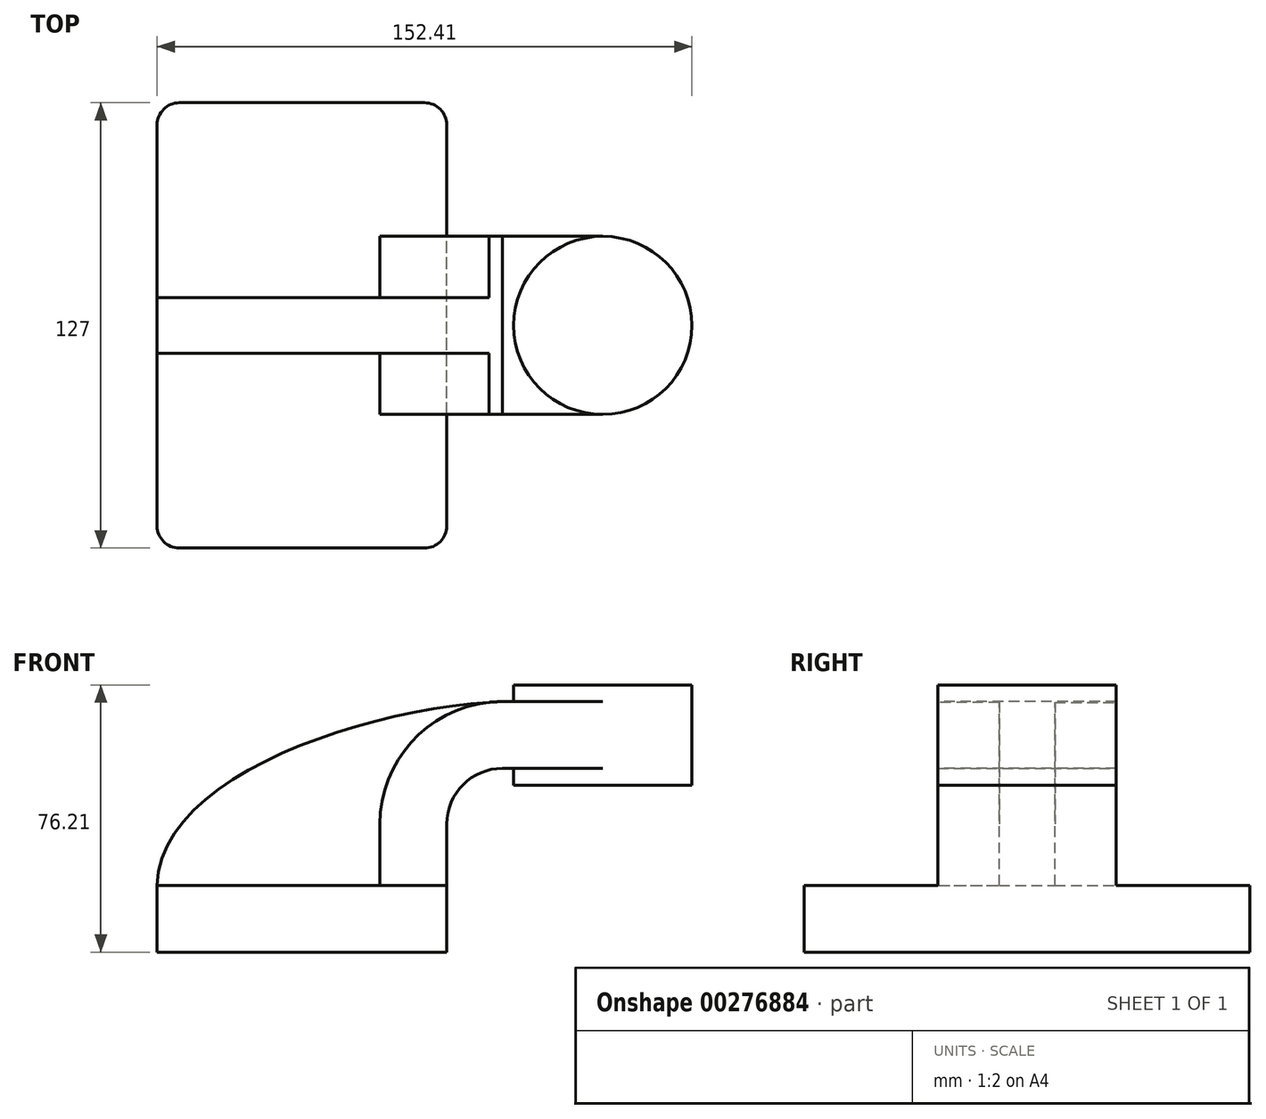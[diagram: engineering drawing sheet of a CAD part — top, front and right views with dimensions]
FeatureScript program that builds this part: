
annotation { "Feature Type Name" : "Feature", "Feature Type Description" : "" }
export const myFeature = defineFeature(function(context is Context, id is Id, definition is map)
    precondition{}
    {
        {
            var Q0;
            Q0=qCreatedBy(makeId("Front.planeOp"),FACE);
            var sketch = newSketch(context, id + "F0", { "sketchPlane" : qUnion([Q0])});
            skLineSegment(sketch, "E0.bottom", {"start": v(41.28, -9.52) * mm, "end": v(-41.28, -9.53) * mm});
            skLineSegment(sketch, "E0.top", {"start": v(41.28, 9.53) * mm, "end": v(-41.28, 9.53) * mm});
            skLineSegment(sketch, "E0.left", {"start": v(41.28, -9.52) * mm, "end": v(41.28, 9.53) * mm});
            skLineSegment(sketch, "E0.right", {"start": v(-41.28, -9.53) * mm, "end": v(-41.28, 9.53) * mm});
            skPoint(sketch, "E0.middle", {"position": v(0, 0) * mm});
            skLineSegment(sketch, "E1.bottom", {"start": v(111.12, 38.1) * mm, "end": v(60.32, 38.1) * mm});
            skLineSegment(sketch, "E1.top", {"start": v(111.12, 66.68) * mm, "end": v(60.32, 66.68) * mm});
            skLineSegment(sketch, "E1.left", {"start": v(111.12, 38.1) * mm, "end": v(111.12, 66.68) * mm});
            skLineSegment(sketch, "E1.right", {"start": v(60.32, 38.1) * mm, "end": v(60.32, 66.67) * mm});
            skPoint(sketch, "E1.middle", {"position": v(85.72, 52.39) * mm});
            skLineSegment(sketch, "E2", {"start": v(41.28, 9.53) * mm, "end": v(41.28, 27) * mm});
            skArc(sketch, "E3", {"start": v(41.27, 27) * mm, "mid": v(45.92, 38.23) * mm, "end": v(57.15, 42.88) * mm});
            skLineSegment(sketch, "E4", {"start": v(57.15, 42.88) * mm, "end": v(85.72, 42.88) * mm});
            skLineSegment(sketch, "E5.0", {"start": v(57.15, 61.93) * mm, "end": v(85.72, 61.93) * mm});
            skArc(sketch, "E5.1", {"start": v(22.23, 27) * mm, "mid": v(32.45, 51.7) * mm, "end": v(57.15, 61.93) * mm});
            skLineSegment(sketch, "E5.2", {"start": v(22.22, 9.53) * mm, "end": v(22.22, 27) * mm});
            skLineSegment(sketch, "E6", {"start": v(85.72, 61.93) * mm, "end": v(85.72, 42.88) * mm});
            skFitSpline(sketch, "E7", {"points": [v(-41.28, 9.52) * mm, v(57.15, 61.93) * mm], "startDerivative": vector(1.48, 94.14) * mm, "endDerivative": vector(114.79, 4.76) * mm});
            skLineSegment(sketch, "E8", {"start": v(85.72, 61.93) * mm, "end": v(85.72, 66.67) * mm});
            skLineSegment(sketch, "E9", {"start": v(85.72, 42.88) * mm, "end": v(85.72, 38.1) * mm});
            skSolve(sketch);
        }
        {
            var Q0;
            Q0=makeQuery(id+"F0.imprint","IMPRINT",FACE,{"disambiguationData":[TD([[makeQuery(id+"F0.imprint","IMPRINT",EDGE,{"derivedFrom":sQuery(id+"F0.wireOp",EDGE,"E0.bottom")}),-1.0]])]});
            extrude(context, id + "F1", {"entities" : qUnion([Q0]), "endBound" : BoundingType.SYMMETRIC, "depth" : 127 * mm});
        }
        {
            var Q0;
            {var subQ1=sQuery(id+"F0.wireOp",EDGE,"E2");Q0=makeQuery(id+"F0.imprint","IMPRINT",FACE,{"disambiguationData":[TD([[makeQuery(id+"F0.imprint","IMPRINT",EDGE,{"derivedFrom":subQ1}),1.0]])]});}
            var Q1;
            {var subQ5=sQuery(id+"F0.wireOp",EDGE,"E6");Q1=makeQuery(id+"F0.imprint","IMPRINT",FACE,{"disambiguationData":[TD([[makeQuery(id+"F0.imprint","IMPRINT",EDGE,{"derivedFrom":subQ5}),-1.0]])]});}
            extrude(context, id + "F2", {"entities" : qUnion([Q0, Q1]), "operationType" : NewBodyOperationType.ADD, "endBound" : BoundingType.SYMMETRIC, "depth" : 50.8 * mm});
        }
        {
            var Q0;
            {var subQ3=sQuery(id+"F0.wireOp",EDGE,"E5.2");Q0=makeQuery(id+"F0.imprint","IMPRINT",FACE,{"disambiguationData":[TD([[makeQuery(id+"F0.imprint","IMPRINT",EDGE,{"derivedFrom":subQ3}),1.0]])]});}
            extrude(context, id + "F3", {"entities" : qUnion([Q0]), "operationType" : NewBodyOperationType.ADD, "endBound" : BoundingType.SYMMETRIC, "depth" : 15.88 * mm});
        }
        {
            var Q0;
            {var subQ0=sQuery(id+"F0.wireOp",EDGE,"E1.left");Q0=makeQuery(id+"F0.imprint","IMPRINT",FACE,{"disambiguationData":[TD([[makeQuery(id+"F0.imprint","IMPRINT",EDGE,{"derivedFrom":subQ0}),1.0]])]});}
            var Q1;
            Q1=sQuery(id+"F0.wireOp",EDGE,"E6");
            revolve(context, id + "F4", {"operationType" : NewBodyOperationType.ADD, "entities" : qUnion([Q0]), "axis" : qUnion([Q1]), "revolveType" : RevolveType.FULL});
        }
        {
            var Q0;
            Q0=makeQuery(id+"F1.opExtrude","CAP_EDGE",EDGE,{"disambiguationData":[OSD([sQuery(id+"F0.wireOp",EDGE,"E0.left")])],"isStart":false});
            var Q1;
            Q1=makeQuery(id+"F1.opExtrude","CAP_EDGE",EDGE,{"disambiguationData":[OSD([sQuery(id+"F0.wireOp",EDGE,"E0.right")])],"isStart":false});
            var Q2;
            Q2=makeQuery(id+"F1.opExtrude","CAP_EDGE",EDGE,{"disambiguationData":[OSD([sQuery(id+"F0.wireOp",EDGE,"E0.left")])],"isStart":true});
            var Q3;
            Q3=makeQuery(id+"F1.opExtrude","CAP_EDGE",EDGE,{"disambiguationData":[OSD([sQuery(id+"F0.wireOp",EDGE,"E0.right")])],"isStart":true});
            fillet(context, id + "F5", {"entities" : qUnion([Q0, Q1, Q2, Q3]), "radius" : 6.35 * mm, "tangentPropagation" : true, "allowEdgeOverflow" : false});
        }
    });
